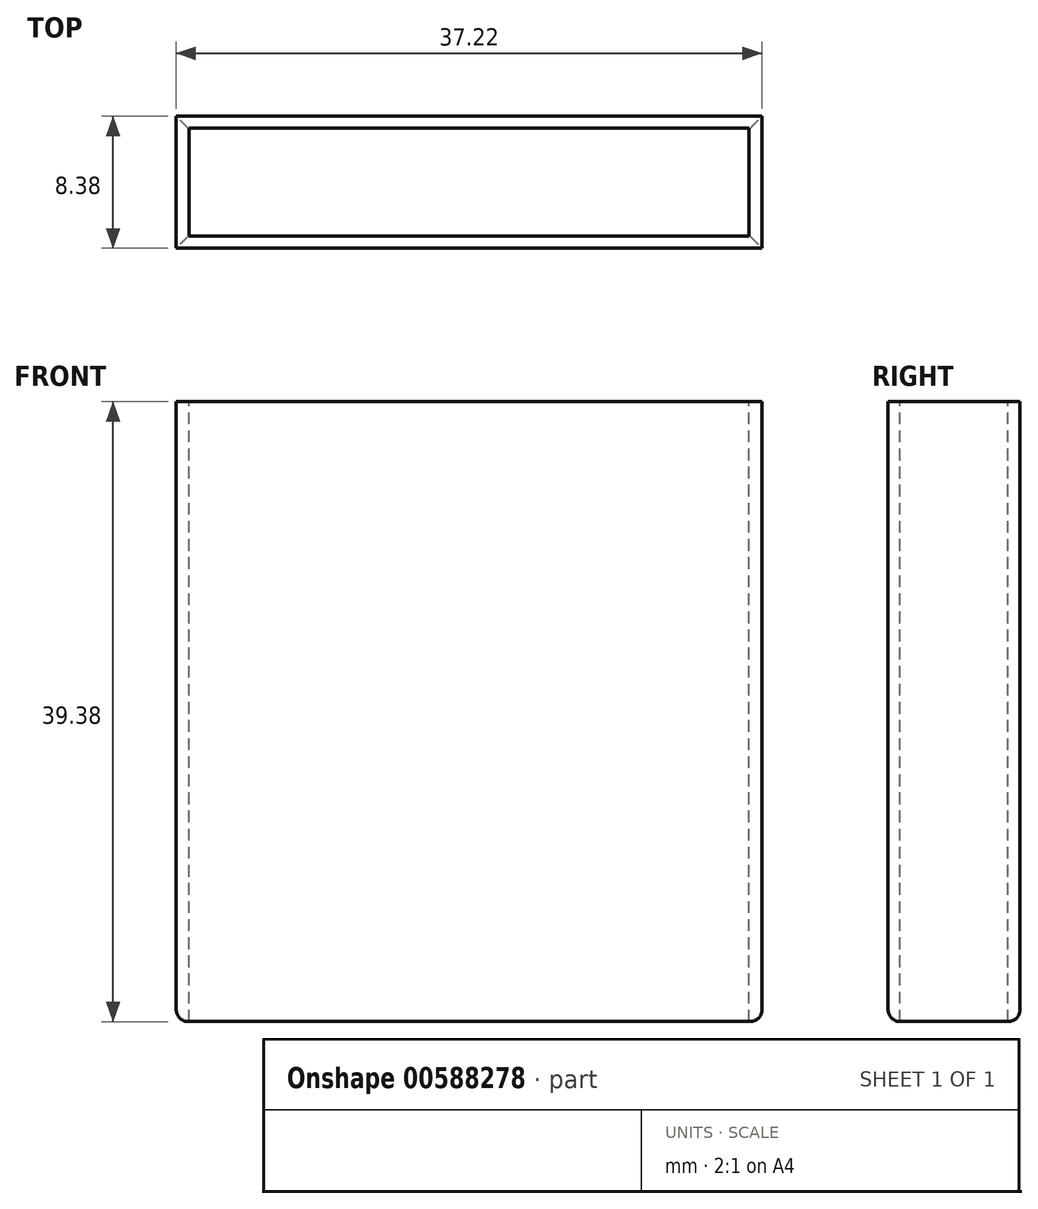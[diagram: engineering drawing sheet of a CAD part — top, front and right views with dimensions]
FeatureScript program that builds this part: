
annotation { "Feature Type Name" : "Feature", "Feature Type Description" : "" }
export const myFeature = defineFeature(function(context is Context, id is Id, definition is map)
    precondition{}
    {
        {
            var Q0;
            Q0=qCreatedBy(makeId("Front.planeOp"),FACE);
            var sketch = newSketch(context, id + "F0", { "sketchPlane" : qUnion([Q0])});
            skLineSegment(sketch, "E0.bottom", {"start": v(-18.6, 19.69) * mm, "end": v(18.6, 19.69) * mm});
            skLineSegment(sketch, "E0.top", {"start": v(-18.6, -19.68) * mm, "end": v(18.6, -19.68) * mm});
            skLineSegment(sketch, "E0.left", {"start": v(-18.6, 19.69) * mm, "end": v(-18.6, -19.68) * mm});
            skLineSegment(sketch, "E0.right", {"start": v(18.6, 19.69) * mm, "end": v(18.6, -19.68) * mm});
            skPoint(sketch, "E0.middle", {"position": v(0, 0) * mm});
            skSolve(sketch);
        }
        {
            var Q0;
            Q0=makeQuery(id+"F0.imprint","IMPRINT",FACE,{"disambiguationData":[TD([[makeQuery(id+"F0.imprint","IMPRINT",EDGE,{"derivedFrom":sQuery(id+"F0.wireOp",EDGE,"E0.bottom")}),-1.0]])]});
            extrude(context, id + "F1", {"entities" : qUnion([Q0]), "endBound" : BoundingType.SYMMETRIC, "depth" : 8.38 * mm, "offsetDistance" : 25.4 * mm});
        }
        {
            var Q0;
            Q0=makeQuery(id+"F1.opExtrude","SWEPT_FACE",FACE,{"disambiguationData":[OSD([sQuery(id+"F0.wireOp",EDGE,"E0.bottom")])]});
            var sketch = newSketch(context, id + "F2", { "sketchPlane" : qUnion([Q0])});
            skLineSegment(sketch, "E1.bottom", {"start": v(17.78, 3.43) * mm, "end": v(-17.78, 3.43) * mm});
            skLineSegment(sketch, "E1.top", {"start": v(17.78, -3.43) * mm, "end": v(-17.78, -3.43) * mm});
            skLineSegment(sketch, "E1.left", {"start": v(17.78, 3.43) * mm, "end": v(17.78, -3.43) * mm});
            skLineSegment(sketch, "E1.right", {"start": v(-17.78, 3.43) * mm, "end": v(-17.78, -3.43) * mm});
            skPoint(sketch, "E1.middle", {"position": v(0, 0) * mm});
            skSolve(sketch);
        }
        {
            var Q0;
            Q0=makeQuery(id+"F2.imprint","IMPRINT",FACE,{"disambiguationData":[TD([[makeQuery(id+"F2.imprint","IMPRINT",EDGE,{"derivedFrom":sQuery(id+"F2.wireOp",EDGE,"E1.bottom")}),1.0]])]});
            extrude(context, id + "F3", {"entities" : qUnion([Q0]), "operationType" : NewBodyOperationType.REMOVE, "oppositeDirection" : true, "depth" : 39.37 * mm, "offsetDistance" : 25.4 * mm});
        }
        {
            var Q0;
            Q0=makeQuery(id+"F1.opExtrude","CAP_EDGE",EDGE,{"disambiguationData":[OSD([sQuery(id+"F0.wireOp",EDGE,"E0.top")])],"isStart":false});
            var Q1;
            Q1=makeQuery(id+"F1.opExtrude","SWEPT_EDGE",EDGE,{"disambiguationData":[OSD([sQuery(id+"F0.wireOp",EDGE,"E0.top"),sQuery(id+"F0.wireOp",EDGE,"E0.right")])]});
            var Q2;
            Q2=makeQuery(id+"F1.opExtrude","CAP_EDGE",EDGE,{"disambiguationData":[OSD([sQuery(id+"F0.wireOp",EDGE,"E0.top")])],"isStart":true});
            var Q3;
            Q3=makeQuery(id+"F1.opExtrude","SWEPT_EDGE",EDGE,{"disambiguationData":[OSD([sQuery(id+"F0.wireOp",EDGE,"E0.top"),sQuery(id+"F0.wireOp",EDGE,"E0.left")])]});
            fillet(context, id + "F4", {"entities" : qUnion([Q0, Q1, Q2, Q3]), "radius" : 0.76 * mm, "tangentPropagation" : true, "allowEdgeOverflow" : false});
        }
    });
